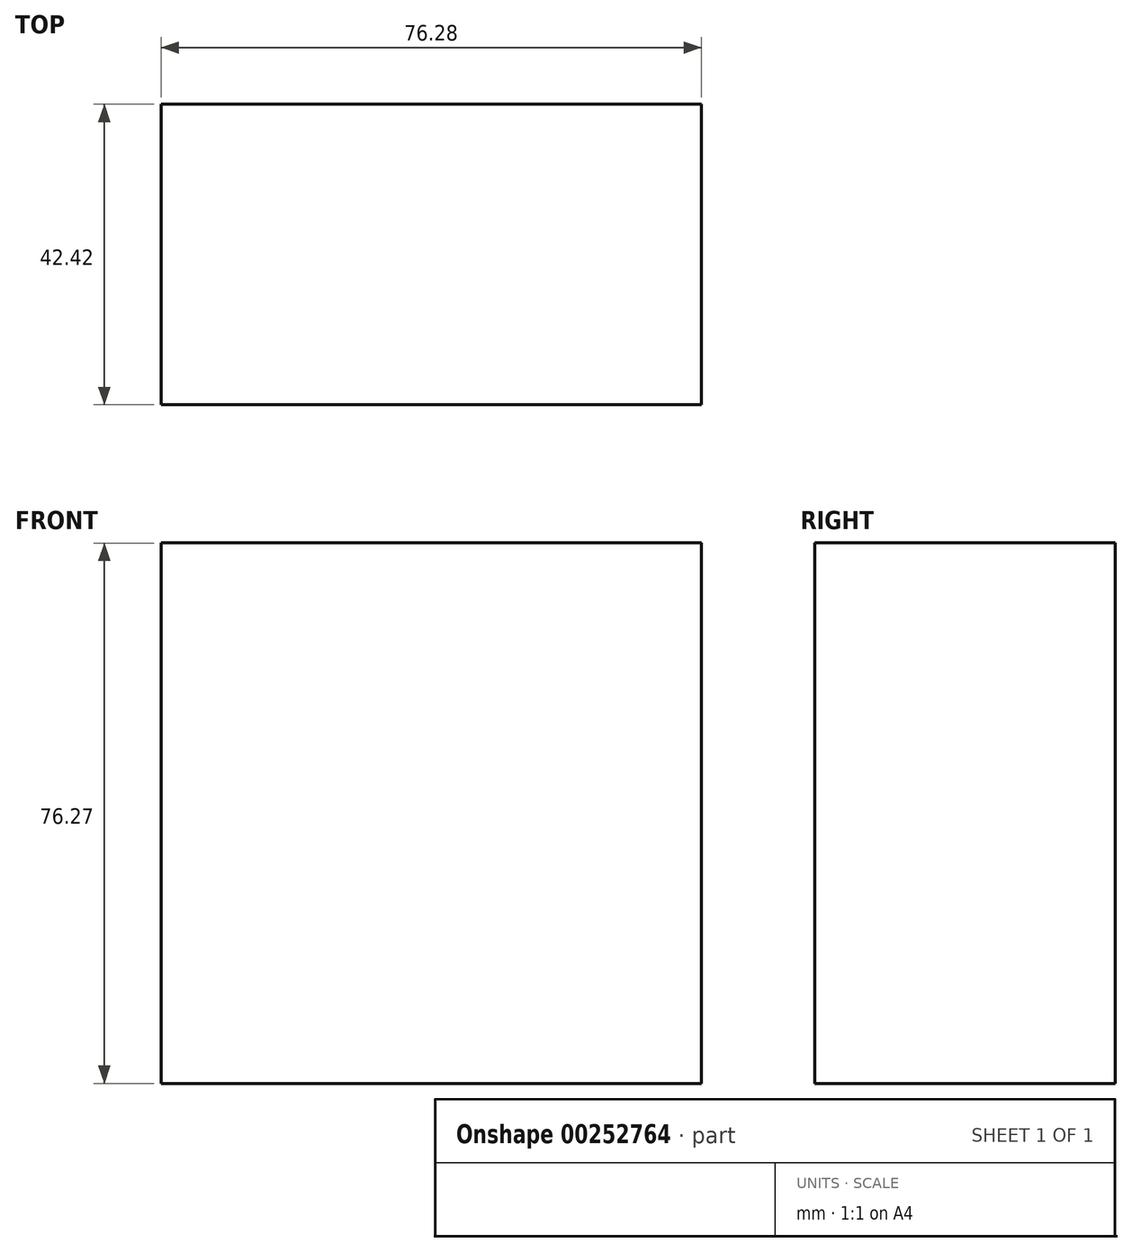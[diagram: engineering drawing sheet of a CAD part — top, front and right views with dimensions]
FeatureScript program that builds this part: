
annotation { "Feature Type Name" : "Feature", "Feature Type Description" : "" }
export const myFeature = defineFeature(function(context is Context, id is Id, definition is map)
    precondition{}
    {
        {
            var Q0;
            Q0=qCreatedBy(makeId("Front.planeOp"),FACE);
            var sketch = newSketch(context, id + "F0", { "sketchPlane" : qUnion([Q0])});
            skLineSegment(sketch, "E0", {"start": v(-64.09, 37.94) * mm, "end": v(-64.09, -38.33) * mm});
            skLineSegment(sketch, "E1", {"start": v(-64.09, 37.94) * mm, "end": v(12.19, 37.94) * mm});
            skLineSegment(sketch, "E2", {"start": v(12.19, 37.94) * mm, "end": v(12.19, -38.33) * mm});
            skLineSegment(sketch, "E3", {"start": v(-64.09, -38.33) * mm, "end": v(12.19, -38.33) * mm});
            skSolve(sketch);
        }
        {
            var Q0;
            Q0 = qSketchRegion(id + "F0", true);
            extrude(context, id + "F1", {"entities" : qUnion([Q0]), "depth" : 42.42 * mm});
        }
    });
